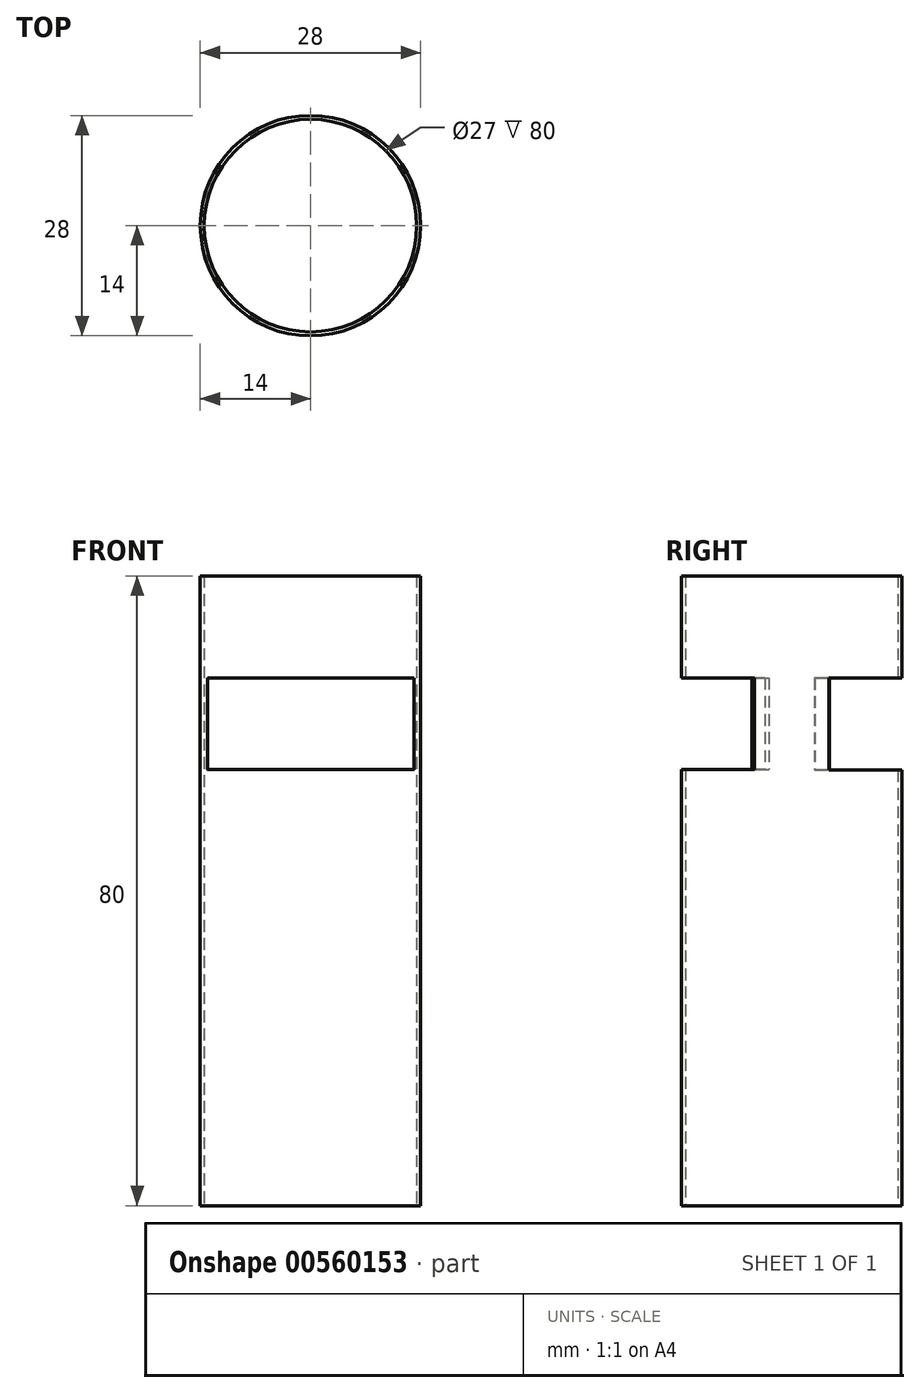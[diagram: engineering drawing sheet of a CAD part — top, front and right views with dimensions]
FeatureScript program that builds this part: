
annotation { "Feature Type Name" : "Feature", "Feature Type Description" : "" }
export const myFeature = defineFeature(function(context is Context, id is Id, definition is map)
    precondition{}
    {
        {
            var Q0;
            Q0=qCreatedBy(makeId("Top.planeOp"),FACE);
            var sketch = newSketch(context, id + "F0", { "sketchPlane" : qUnion([Q0])});
            skCircle(sketch, "E0", {"center": v(0, 0) * mm, "radius": 13.5 * mm});
            skCircle(sketch, "E1", {"center": v(0, 0) * mm, "radius": 14 * mm});
            skSolve(sketch);
        }
        {
            var Q0;
            Q0 = qSketchRegion(id + "F0", true);
            extrude(context, id + "F1", {"entities" : qUnion([Q0]), "depth" : 80 * mm, "offsetDistance" : 25.4 * mm});
        }
        {
            var Q0;
            Q0=qCreatedBy(makeId("Front.planeOp"),FACE);
            var sketch = newSketch(context, id + "F2", { "sketchPlane" : qUnion([Q0])});
            skLineSegment(sketch, "E2.bottom", {"start": v(-13.17, 67.04) * mm, "end": v(13.19, 67.04) * mm});
            skLineSegment(sketch, "E2.top", {"start": v(-13.17, 55.33) * mm, "end": v(13.19, 55.33) * mm});
            skLineSegment(sketch, "E2.left", {"start": v(-13.17, 67.04) * mm, "end": v(-13.17, 55.33) * mm});
            skLineSegment(sketch, "E2.right", {"start": v(13.19, 67.04) * mm, "end": v(13.19, 55.33) * mm});
            skSolve(sketch);
        }
        {
            var Q0;
            Q0 = qSketchRegion(id + "F2", true);
            extrude(context, id + "F3", {"entities" : qUnion([Q0]), "operationType" : NewBodyOperationType.REMOVE, "oppositeDirection" : true, "depth" : 25.4 * mm, "offsetDistance" : 25.4 * mm});
        }
        {
            var Q0;
            Q0=qCreatedBy(makeId("Front.planeOp"),FACE);
            var sketch = newSketch(context, id + "F4", { "sketchPlane" : qUnion([Q0])});
            skLineSegment(sketch, "E3.bottom", {"start": v(-13.06, 67.05) * mm, "end": v(13.18, 67.05) * mm});
            skLineSegment(sketch, "E3.top", {"start": v(-13.06, 55.44) * mm, "end": v(13.18, 55.44) * mm});
            skLineSegment(sketch, "E3.left", {"start": v(-13.06, 67.05) * mm, "end": v(-13.06, 55.44) * mm});
            skLineSegment(sketch, "E3.right", {"start": v(13.18, 67.05) * mm, "end": v(13.18, 55.44) * mm});
            skSolve(sketch);
        }
        {
            var Q0;
            Q0 = qSketchRegion(id + "F4", true);
            extrude(context, id + "F5", {"entities" : qUnion([Q0]), "operationType" : NewBodyOperationType.REMOVE, "depth" : 25.4 * mm, "offsetDistance" : 25.4 * mm});
        }
    });
